# Revit family: PIANO S
name_source: partatom
category: Осветительные приборы
revit_build: Autodesk Revit 2016 (Build: 20150220_1215(x64)
units: mm (PartAtom-declared; Revit-internal decimal feet)

## family parameters
Источник света = Да
Общий = Нет
Основа = Грань
При загрузке вырезать с полостями = Нет
Размер круглого соединителя = Использовать диаметр
Тип детали = Нормальный
Точка расчета площади = Нет

## types (1)
- PIANO S
    ADSK_Единица измерения = Шт.
    ADSK_Завод-изготовитель = ООО МГК Световые технологии
    ADSK_Количество фаз = 1
    ADSK_Количество фаз числовое = 1
    ADSK_Коэффициент мощности = 0.8
    ADSK_Масса = 0
    ADSK_Наименование = Встраиваемый светильник, создающий прямое диффузное освещение, световод по периметру подсвечивает потолок. Корпус светильника изготовлен из алюминия, окрашенного порошковой краской. Оптическая часть закрыта молочным темперированным стеклом, световод изготовлен из прозрачного темперированного стекла
    ADSK_Напряжение = 230 В
    ADSK_Номинальная мощность = 0 кВт
    ADSK_Полная мощность = 0 кВ·А
    ADSK_Размер_Высота = 40 мм
    ADSK_Размер_Длина = 100 мм
    ADSK_Размер_Ширина = 100 мм
    ADSK_Ток = 0 А
    ADSK_Энергоэффективность = 0 лм/Вт
    IP Class = IP40
    URL = http://www.ltcompany.com
    Блок аварийного питания = Нет
    Видимая форма излучения при визуализации = Нет
    Группа модели = Светильники
    Декор = Корпус металл
    Изготовитель = ООО МГК Световые технологии
    Излучение по длине прямоугольника = 69 мм
    Излучение по ширине прямоугольника = 69 мм
    Класс Защиты = II
    Климатическая зона = УХЛ4
    Код по классификатору = D5020200
    Корпус = Корпус черный пластик
    Область использования = Гостиницы, Индивидуальные дома, Культурно-развлекательные, Магазины/Бутики, Объекты бытового обслуживания, Объекты общественного питания, Офисы, ТРЦ
    Описание = Встраиваемый светильник, создающий прямое диффузное освещение, световод по периметру подсвечивает потолок. Корпус светильника изготовлен из алюминия, окрашенного порошковой краской. Оптическая часть закрыта молочным темперированным стеклом, световод изготовлен из прозрачного темперированного стекла
    Отметка по умолчанию = 0 мм
    Плафон = Плафон самосвечение
    Полная установленная мощность = 0 кВ·А
    Разработчик = ООО ПРОРУБИМ
    Разработчик (телефон) = +7 (495) 649-85-43
    Светофильтр = 16777215
    Смещение цветовой температуры при затухании лампы = <Нет>
    Тип ИС = LED
    Тип ПРА = Драйвер
    Тип продукции = Светильники
    Угол наклона = -90.00°
    Установочная длина = 44 мм
    Установочная ширина = 44 мм
    Файл фотометрической сетки = generic
